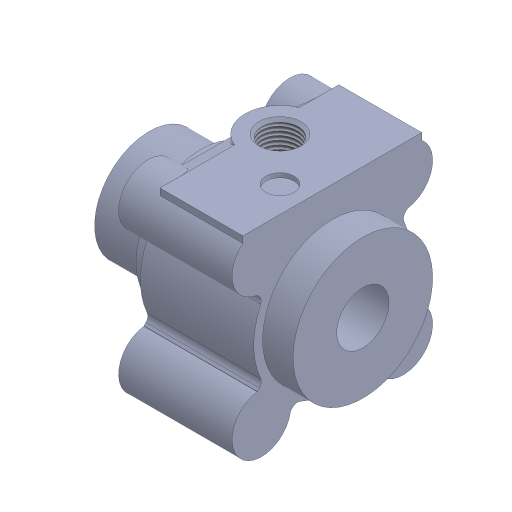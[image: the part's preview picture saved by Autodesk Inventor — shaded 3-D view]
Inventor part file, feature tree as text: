
AUTODESK INVENTOR PART (.ipt)
format: ipt  version: 2024.3 (Build 283343000, 343)  size: 363,008 bytes
history: native  units: mm
features: other x42, sketch x25, extrude x14, hole x11
ambient origin geometry x8: Origin, YZ Plane, XZ Plane, XY Plane, X Axis, Y Axis, Z Axis, Center Point
bodies: Solid1 (feature_tree)
feature tree (92):
  extrude  "Extrusion1"  Depth=7.0mm TaperAngle=0.0deg
  extrude  "Extrusion2"  Depth=16.0mm TaperAngle=0.0deg
  extrude  "Extrusion3"  Depth=5.0mm TaperAngle=0.0deg
  extrude  "Extrusion4"  Depth=20.0mm TaperAngle=0.0deg
  extrude  "Extrusion5"  Depth=20.0mm TaperAngle=0.0deg
  extrude  "Extrusion6"  Depth=20.0mm TaperAngle=0.0deg
  hole  "Hole1"  [1 undecoded]
  hole  "Hole2"  [1 undecoded]
  extrude  "Extrusion7"  Depth=4.5mm TaperAngle=0.0deg
  hole  "Hole3"  [1 undecoded]
  extrude  "Extrusion8"  TaperAngle=0.0deg  [1 undecoded]
  hole  "Hole4"  [1 undecoded]
  extrude  "Extrusion9"  Depth=25.0mm
  hole  "Hole5"  [1 undecoded]
  extrude  "Extrusion10"  [1 undecoded]
  extrude  "Extrusion11"  [1 undecoded]
  extrude  "Extrusion12"  [1 undecoded]
  extrude  "Extrusion13"  [1 undecoded]
  extrude  "Extrusion14"  [1 undecoded]
  hole  "Hole6"  [1 undecoded]
  hole  "Hole7"  [1 undecoded]
  hole  "Hole8"  [1 undecoded]
  hole  "Hole9"  [1 undecoded]
  hole  "Hole10"  [1 undecoded]
  hole  "Hole11"  [1 undecoded]
  other  "BELLOW_XY"
  other  "BELLOW_YZ"
  other  "BELLOW_ZX"
  other  "BELLOW_X"
  other  "BELLOW_Y"
  other  "BELLOW_Z"
  other  "BELLOW_Center"
  other  "accessories_XY"
  other  "accessories_YZ"
  other  "accessories_ZX"
  other  "accessories_X"
  other  "accessories_Y"
  other  "accessories_Z"
  other  "accessories_Center"
  other  "br_l_XY"
  other  "br_l_YZ"
  other  "br_l_ZX"
  other  "br_l_X"
  other  "br_l_Y"
  other  "br_l_Z"
  other  "br_l_Center"
  other  "fitting_XY"
  other  "fitting_YZ"
  other  "fitting_ZX"
  other  "fitting_X"
  other  "fitting_Y"
  other  "fitting_Z"
  other  "fitting_Center"
  other  "rod_XY"
  other  "rod_YZ"
  other  "rod_ZX"
  other  "rod_X"
  other  "rod_Y"
  other  "rod_Z"
  other  "rod_Center"
  other  "start_XY"
  other  "start_YZ"
  other  "start_ZX"
  other  "start_X"
  other  "start_Y"
  other  "start_Z"
  other  "start_Center"
  sketch  "Sketch_1"  dims[d0=26.0mm d1=0.0mm d2=7.0mm d3=0.0mm]
  sketch  "Sketch_2"  dims[d4=4.0mm d5=0.0mm d6=16.0mm d7=0.0mm]
  sketch  "Sketch_3"  dims[d8=32.5mm d9=0.0mm d10=5.0mm d11=0.0mm]
  sketch  "Sketch_4"  dims[d12=6.5mm d13=6.0mm d14=4.0mm d15=2.0mm d16=90.0deg d17=1.0mm d18=0.0mm]
  sketch  "Sketch_6"  dims[d28=10.5mm d29=6.0mm d30=4.0mm d31=2.0mm d32=90.0deg d33=0.5mm d34=0.0mm d35=20.0mm d36=0.0mm]
  sketch  "Sketch_5"  dims[d19=10.5mm d20=6.0mm d21=4.0mm d22=2.0mm d23=90.0deg d24=0.5mm d25=0.0mm d26=20.0mm d27=0.0mm]
  sketch  "Sketch7"  dims[d37=10.5mm d38=6.0mm d39=4.0mm d40=2.0mm d41=90.0deg d42=0.5mm d43=0.0mm d44=20.0mm d45=0.0mm]
  sketch  "Sketch8"  dims[d46=10.5mm d47=6.0mm d48=4.0mm d49=2.0mm d50=90.0deg d51=0.5mm d52=0.0mm d53=20.0mm d54=0.0mm]
  sketch  "Sketch_17"  dims[d100=12.0mm d101=6.0mm d102=4.0mm d103=2.0mm d104=90.0deg d105=49.0mm d106=0.0mm d107=0.0mm]
  sketch  "Sketch10"  dims[d55=4.5mm d56=0.0mm d57=4.5mm d58=0.0mm]
  sketch  "Sketch_18"  dims[d108=0.0mm d109=0.0mm]
  sketch  "Sketch12"  dims[d59=4.5mm d60=0.0mm d61=4.5mm d62=0.0mm]
  sketch  "Sketch_19"  dims[d110=0.0mm d111=0.0mm]
  sketch  "Sketch14"  dims[d72=4.917mm d73=10.0mm d74=6.0mm d75=2.0mm d76=90.0deg d77=12.0mm d78=120.0deg]
  sketch  "Sketch_20"  dims[d112=0.0mm d113=25.0mm]
  sketch  "Sketch_13"  dims[d63=8.0mm d64=7.4mm d65=0.624793mm d66=7.985mm d67=9.728mm d68=2.0mm d69=90.0deg d70=10.0mm d71=120.0deg]
  sketch  "Sketch_14"  dims[d79=4.917mm d80=10.0mm d81=6.0mm d82=2.0mm d83=90.0deg d84=12.0mm d85=120.0deg]
  sketch  "Sketch_15"  dims[d86=4.917mm d87=10.0mm d88=6.0mm d89=2.0mm d90=90.0deg d91=12.0mm d92=120.0deg]
  sketch  "Sketch_16"  dims[d93=4.917mm d94=10.0mm d95=6.0mm d96=2.0mm d97=90.0deg d98=12.0mm d99=120.0deg]
  sketch  "Sketch20"
  sketch  "Sketch21"
  sketch  "Sketch22"
  sketch  "Sketch23"
  sketch  "Sketch24"
  sketch  "Sketch25"
note: 17 required parameter values undecoded (feature->parameter linkage not recoverable at this tier; creation-order binding heuristic only, values carry confidence <= 0.55)
